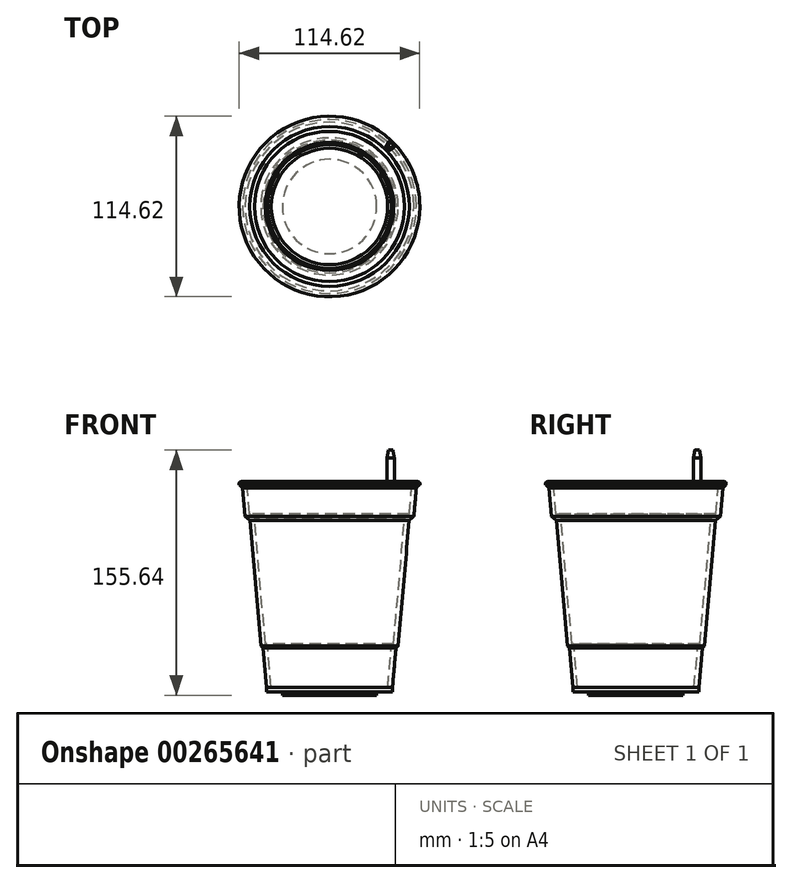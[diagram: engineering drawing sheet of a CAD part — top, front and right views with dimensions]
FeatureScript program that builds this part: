
annotation { "Feature Type Name" : "Feature", "Feature Type Description" : "" }
export const myFeature = defineFeature(function(context is Context, id is Id, definition is map)
    precondition{}
    {
        {
            var Q0;
            Q0=qCreatedBy(makeId("Front.planeOp"),FACE);
            var sketch = newSketch(context, id + "F0", { "sketchPlane" : qUnion([Q0])});
            skLineSegment(sketch, "E0", {"start": v(0, 0) * mm, "end": v(40, 0) * mm});
            skLineSegment(sketch, "E1", {"start": v(40, 0) * mm, "end": v(40, 3) * mm});
            skLineSegment(sketch, "E2", {"start": v(40, 3) * mm, "end": v(42.18, 27.9) * mm});
            skLineSegment(sketch, "E3", {"start": v(42.18, 27.9) * mm, "end": v(43.6, 29.32) * mm});
            skLineSegment(sketch, "E4", {"start": v(43.6, 29.32) * mm, "end": v(50.57, 109.01) * mm});
            skLineSegment(sketch, "E5", {"start": v(47.68, 110.46) * mm, "end": v(40.7, 30.67) * mm});
            skLineSegment(sketch, "E6", {"start": v(40.7, 30.67) * mm, "end": v(39.29, 29.25) * mm});
            skLineSegment(sketch, "E7", {"start": v(39.29, 29.25) * mm, "end": v(36.99, 3) * mm});
            skLineSegment(sketch, "E8", {"start": v(36.99, 3) * mm, "end": v(0, 3) * mm});
            skLineSegment(sketch, "E9", {"start": v(0, 3) * mm, "end": v(0, 0) * mm});
            skLineSegment(sketch, "E10", {"start": v(50.57, 109.01) * mm, "end": v(53.57, 111.72) * mm});
            skLineSegment(sketch, "E11", {"start": v(53.57, 111.72) * mm, "end": v(55.31, 131.64) * mm});
            skLineSegment(sketch, "E12", {"start": v(55.31, 131.64) * mm, "end": v(57.31, 131.64) * mm});
            skLineSegment(sketch, "E13", {"start": v(57.31, 131.64) * mm, "end": v(57.31, 133.64) * mm});
            skLineSegment(sketch, "E14", {"start": v(57.31, 133.64) * mm, "end": v(52.48, 133.64) * mm});
            skLineSegment(sketch, "E15", {"start": v(52.48, 133.64) * mm, "end": v(50.69, 113.16) * mm});
            skLineSegment(sketch, "E16", {"start": v(50.69, 113.16) * mm, "end": v(47.68, 110.46) * mm});
            skSolve(sketch);
        }
        {
            var Q0;
            Q0 = qSketchRegion(id + "F0", true);
            var Q1;
            Q1=sQuery(id+"F0.wireOp",EDGE,"E9");
            revolve(context, id + "F1", {"entities" : qUnion([Q0]), "axis" : qUnion([Q1]), "revolveType" : RevolveType.FULL});
        }
        {
            var Q0;
            Q0=makeQuery(id+"F1.opRevolve","SWEPT_FACE",FACE,{"disambiguationData":[OSD([sQuery(id+"F0.wireOp",EDGE,"E0")])]});
            var sketch = newSketch(context, id + "F2", { "sketchPlane" : qUnion([Q0])});
            skCircle(sketch, "E17", {"center": v(0, 0) * mm, "radius": 30 * mm});
            skSolve(sketch);
        }
        {
            var Q0;
            Q0 = qSketchRegion(id + "F2", true);
            extrude(context, id + "F3", {"entities" : qUnion([Q0]), "operationType" : NewBodyOperationType.ADD, "depth" : 2 * mm});
        }
        {
            var Q0;
            Q0=makeQuery(id+"F1.opRevolve","SWEPT_FACE",FACE,{"disambiguationData":[OSD([sQuery(id+"F0.wireOp",EDGE,"E14")])]});
            var sketch = newSketch(context, id + "F4", { "sketchPlane" : qUnion([Q0])});
            skLineSegment(sketch, "E18", {"start": v(0, 0) * mm, "end": v(57.31, 0) * mm, "construction": true});
            skLineSegment(sketch, "E19", {"start": v(0, 0) * mm, "end": v(40.53, 40.53) * mm, "construction": true});
            skCircle(sketch, "E20", {"center": v(38.82, 38.82) * mm, "radius": 2.42 * mm});
            skSolve(sketch);
        }
        {
            var Q0;
            Q0 = qSketchRegion(id + "F4", true);
            extrude(context, id + "F5", {"entities" : qUnion([Q0]), "operationType" : NewBodyOperationType.ADD, "depth" : 20 * mm});
        }
        {
            var Q0;
            Q0=makeQuery(id+"F1.opRevolve","SWEPT_EDGE",EDGE,{"disambiguationData":[OSD([sQuery(id+"F0.wireOp",EDGE,"E13"),sQuery(id+"F0.wireOp",EDGE,"E14")])]});
            var Q1;
            Q1=makeQuery(id+"F1.opRevolve","SWEPT_EDGE",EDGE,{"disambiguationData":[OSD([sQuery(id+"F0.wireOp",EDGE,"E14"),sQuery(id+"F0.wireOp",EDGE,"E15")])]});
            fillet(context, id + "F6", {"entities" : qUnion([Q0, Q1]), "radius" : 1 * mm, "tangentPropagation" : true, "allowEdgeOverflow" : false});
        }
        {
            var Q0;
            Q0=makeQuery(id+"F1.opRevolve","SWEPT_EDGE",EDGE,{"disambiguationData":[OSD([sQuery(id+"F0.wireOp",EDGE,"E11"),sQuery(id+"F0.wireOp",EDGE,"E12")])]});
            chamfer(context, id + "F7", {"entities" : qUnion([Q0]), "width" : 2 * mm, "tangentPropagation" : true});
        }
        {
            var Q0;
            Q0=makeQuery(id+"F5.opExtrude","CAP_EDGE",EDGE,{"disambiguationData":[OSD([sQuery(id+"F4.wireOp",EDGE,"E20")])],"isStart":false});
            chamfer(context, id + "F8", {"entities" : qUnion([Q0]), "chamferType" : ChamferType.TWO_OFFSETS, "width1" : 1 * mm, "oppositeDirection" : false, "width2" : 5 * mm, "tangentPropagation" : true});
        }
    });
